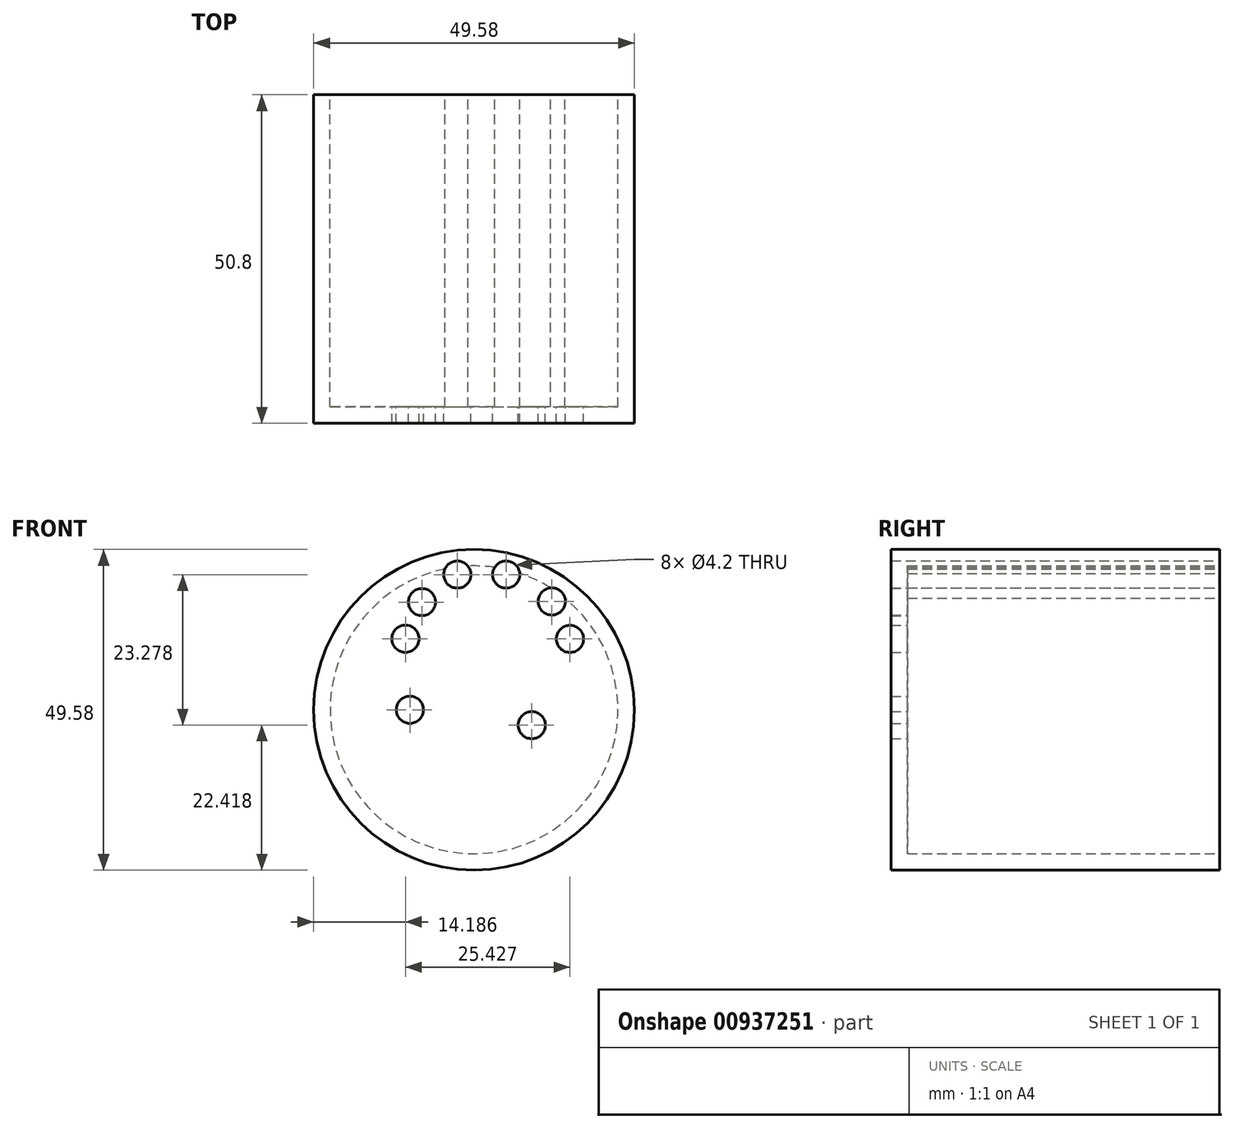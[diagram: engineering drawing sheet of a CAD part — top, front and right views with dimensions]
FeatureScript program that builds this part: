
annotation { "Feature Type Name" : "Feature", "Feature Type Description" : "" }
export const myFeature = defineFeature(function(context is Context, id is Id, definition is map)
    precondition{}
    {
        {
            var Q0;
            Q0=qCreatedBy(makeId("Front.planeOp"),FACE);
            var sketch = newSketch(context, id + "F0", { "sketchPlane" : qUnion([Q0])});
            skCircle(sketch, "E0", {"center": v(0, 0) * mm, "radius": 24.79 * mm});
            skSolve(sketch);
        }
        {
            var Q0;
            Q0 = qSketchRegion(id + "F0", true);
            extrude(context, id + "F1", {"entities" : qUnion([Q0]), "depth" : 50.8 * mm, "offsetDistance" : 25.4 * mm});
        }
        {
            var Q0;
            Q0=makeQuery(id+"F1.opExtrude","CAP_FACE",FACE,{"disambiguationData":[OSD([sQuery(id+"F0.wireOp",EDGE,"E0")])],"isStart":true});
            shell(context, id + "F2", {"entities" : qUnion([Q0]), "thickness" : 2.54 * mm});
        }
        {
            var Q0;
            Q0=qCreatedBy(makeId("Front.planeOp"),FACE);
            var sketch = newSketch(context, id + "F3", { "sketchPlane" : qUnion([Q0])});
            skLineSegment(sketch, "E1.bottom", {"start": v(-24.6, 25.2) * mm, "end": v(24.6, 25.2) * mm});
            skLineSegment(sketch, "E1.top", {"start": v(-24.6, -25.2) * mm, "end": v(24.6, -25.2) * mm});
            skLineSegment(sketch, "E1.left", {"start": v(-24.6, 25.2) * mm, "end": v(-24.6, -25.2) * mm});
            skLineSegment(sketch, "E1.right", {"start": v(24.6, 25.2) * mm, "end": v(24.6, -25.2) * mm});
            skPoint(sketch, "E1.middle", {"position": v(0, 0) * mm});
            skSolve(sketch);
        }
        {
            var Q0;
            Q0 = qSketchRegion(id + "F3", true);
            var Q1;
            Q1=sQuery(id+"F3.wireOp",EDGE,"E1.right");
            var Q2;
            Q2=sQuery(id+"F3.wireOp",EDGE,"E1.top");
            var Q3;
            Q3=sQuery(id+"F3.wireOp",EDGE,"E1.left");
            var Q4;
            Q4=sQuery(id+"F3.wireOp",EDGE,"E1.bottom");
            extrude(context, id + "F4", {"entities" : qUnion([Q0]), "bodyType" : ToolBodyType.SURFACE, "operationType" : NewBodyOperationType.ADD, "surfaceEntities" : qUnion([Q1, Q2, Q3, Q4]), "depth" : 38.1 * mm, "offsetDistance" : 25.4 * mm});
        }
        {
            var Q0;
            Q0=makeQuery(id+"F4.opExtrude","SWEPT_EDGE",EDGE,{"disambiguationData":[OSD([sQuery(id+"F3.wireOp",VERTEX,"E1.bottom.start")])]});
            var Q1;
            Q1=makeQuery(id+"F4.opExtrude","SWEPT_EDGE",EDGE,{"disambiguationData":[OSD([sQuery(id+"F3.wireOp",VERTEX,"E1.bottom.end")])]});
            var Q2;
            Q2=makeQuery(id+"F4.opExtrude","SWEPT_EDGE",EDGE,{"disambiguationData":[OSD([sQuery(id+"F3.wireOp",VERTEX,"E1.top.end")])]});
            var Q3;
            Q3=makeQuery(id+"F4.opExtrude","SWEPT_EDGE",EDGE,{"disambiguationData":[OSD([sQuery(id+"F3.wireOp",VERTEX,"E1.left.end")])]});
            fillet(context, id + "F5", {"entities" : qUnion([Q0, Q1, Q2, Q3]), "radius" : 5.08 * mm, "tangentPropagation" : true, "allowEdgeOverflow" : false});
        }
        {
            var Q0;
            Q0=qCreatedBy(makeId("Front.planeOp"),FACE);
            var sketch = newSketch(context, id + "F6", { "sketchPlane" : qUnion([Q0])});
            skPoint(sketch, "E2", {"position": v(8.92, -2.37) * mm});
            skPoint(sketch, "E3", {"position": v(-9.92, 0) * mm});
            skPoint(sketch, "E4", {"position": v(14.82, 10.97) * mm});
            skPoint(sketch, "E5", {"position": v(12.02, 16.75) * mm});
            skPoint(sketch, "E6", {"position": v(4.97, 20.9) * mm});
            skPoint(sketch, "E7", {"position": v(-2.59, 20.9) * mm});
            skPoint(sketch, "E8", {"position": v(-8.05, 16.65) * mm});
            skPoint(sketch, "E9", {"position": v(-10.6, 10.98) * mm});
            skSolve(sketch);
        }
        {
            var Q0;
            Q0=sQuery(id+"F6.wireOp",VERTEX,"E2");
            var Q1;
            Q1=sQuery(id+"F6.wireOp",VERTEX,"E4");
            var Q2;
            Q2=sQuery(id+"F6.wireOp",VERTEX,"E5");
            var Q3;
            Q3=sQuery(id+"F6.wireOp",VERTEX,"E6");
            var Q4;
            Q4=sQuery(id+"F6.wireOp",VERTEX,"E7");
            var Q5;
            Q5=sQuery(id+"F6.wireOp",VERTEX,"E8");
            var Q6;
            Q6=sQuery(id+"F6.wireOp",VERTEX,"E9");
            var Q7;
            Q7=sQuery(id+"F6.wireOp",VERTEX,"E3");
            var Q8;
            Q8=makeQuery(id+"F1.opExtrude","SWEPT_BODY",BODY,{"disambiguationData":[OSD([sQuery(id+"F0.wireOp",EDGE,"E0")])]});
            hole(context, id + "F7", {"style" : HoleStyle.SIMPLE, "endStyle" : HoleEndStyle.THROUGH, "oppositeDirection" : true, "standardTappedOrClearance" : lookupTablePath({ "standard" : "ISO", "engagement" : "75%", "pitch" : "0.8 mm", "size" : "M5", "type" : "Tapped" }), "standardBlindInLast" : lookupTablePath({ "standard" : "ISO", "fit" : "Normal", "engagement" : "75%", "pitch" : "0.8 mm", "size" : "M5", "type" : "Clearance & tapped" }), "holeDiameter" : 4.2 * mm, "majorDiameter" : 5 * mm, "showTappedDepth" : true, "isTappedThrough" : true, "tappedDepth" : 12.7 * mm, "tapClearance" : 3, "locations" : qUnion([Q0, Q1, Q2, Q3, Q4, Q5, Q6, Q7]), "scope" : qUnion([Q8])});
        }
    });
